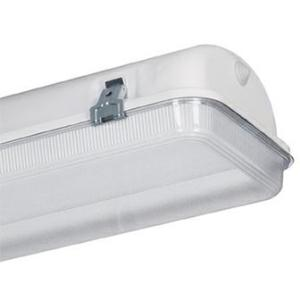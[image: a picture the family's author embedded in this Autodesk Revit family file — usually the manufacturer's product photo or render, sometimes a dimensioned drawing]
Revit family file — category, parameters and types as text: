
# Revit family: 3f_filippi_-_beta_i3f_75_pc_ampio_3f_filippi_-_55596_-_i3f_led_752x12w_ampio_l655
name_source: partatom
category: Lighting Fixtures
units: mm (PartAtom-declared; Revit-internal decimal feet)

## family parameters
Cut with Voids When Loaded = No
Host = Face
Light Source = No
Part Type = Normal
Room Calculation Point = No
Round Connector Dimension = Use Diameter
Shared = No

## types (1)
- 3F Filippi - Beta i3F 75 PC Ampio (1 x LED, 3955 lm, 28 W, 4000 K)
    Apparent Load = 28 VA
    Approval mark = ENEC
    CIE Flux Codes = 52 82 96 97 100
    Color Rendering = 80
    Color Temperature = 4000 K
    Control Gear = Electronic ballast
    Default Elevation = 1800 mm
    Description = ILLUMINOTECHNICAL
Luminous efficiency 100% (DLOR 97%, ULOR 3%).
Initial luminous flux of the luminaire 3955 lm.
Wide symmetric distribution.
Installation Interdistance Transv.D = 1.27 x hu - Long.D = 1.26 x hu.
Tabular UGR (CIE 117 - 4H-8H; S=0.25H; 70/50/20): RUG 20.5 - 22.1.
Beam angle: 92° - 100°.
Luminous efficacy 141 lm/W.
Lifetime (L93/B10): 30000 h. (tq+25°C)
Lifetime (L90/B10): 50000 h. (tq+25°C)
Lifetime (L85/B10): 80000 h. (tq+25°C)
Lifetime (L80/B10): 100000 h. (tq+25°C)
Lifetime (L85/B10): 50000 h. (tq+35°C)
Sudden decreased luminous flux after 50000 hours: 0% (C0).
Photobiological safety in compliance with IEC/TR 62778: RG0 risk exempt, (IEC 62471).
In compliance with IEC/EN 62722-2-1 - IEC/EN 62717 standards.

SOURCE
2 linear LED modules 12W/840.
Energy efficiency class (UE 2019/2020 - UE 2019/2015): D.
CIE 13.3 Colour rendering index: CRI >80 (R9 <50%).
IES TM-30 Fidelity Index: Rf = 84 Rg = 95.
CCT nominal colour temperature 4000 K.
Colour initial tolerance (MacAdam): SDCM 3.

MECHANICAL
Single-piece housing in pressed steel, powder-coated in white epoxy-polyester.
Diffuser in self-extinguishing V2 polycarbonate, photo-engraved interior, UV stabilised, injection moulded, with smooth outer surface, sealing gasket, hinged opening by means of galvanised steel clips.
Wide flow recuperator, oversized, in specular aluminium with superficial titanium-magnesium treatment, non-iridescent.
Gear-tray unit in hot-galvanised steel, painted in white polyester, fixed to the housing by means of "Ribloc" rapid devices in galvanised steel, hinged opening.
Luminaire with limited surface temperature. - D - (EN 60598-2-24)
Dimensions: 655x235 mm, height 140 mm. Weight 3.08 kg.
IP65 protection degree.
Mechanical strength to impacts IK10 (20 joule).
Glow-wire test resistance 850°C.

ELECTRICAL
Halogen Free electronic wiring 230V-50/60Hz, power factor 0.90, THD <25%, constant output current, SELV, class I, 1 driver.
Power of the luminaire 28 W.
CE - IEC 60598-1 - EN 60598-1.
SAFE FLICKER: PstLM=<1 and SVM=<0.4 (IEC TR 61547-1 and IEC TR 63158), to ensure a more comfortable and safe light.
Luminaire compliant with EN 60598-2-22 for power supply from a centralised emergency system CPSS (Central Power Supply System), not incorporated in the luminaire - high risk areas excluded. The default power and flux are 100% in AC and 100% in DC.
Ambient temperature from -20°C to +35°C.
Temperature class T6 max 85°C.
Relative humidity UR: <85%.

INSTALLATION
Ceiling / Suspended / Wall.
All accessories dedicated to this product are available on the Catalog and on our website www.3F-Filippi.com.

APPLICATIONS
Suitable product for food production plants (HACCP), IFS (Food Version 6), BRC (GSFS Food Version 7).
In industrial environments, stores and dry, dusty indoor environments, subject to occasional water splashes.

WARNING
Fixture not suitable for cold stores with an ambient temperature <0°C and/or relative humidity >85%.
Luminaire designed for disposal/recycling at end-of-life.
Replaceable (LED only) light source by a professional. Replaceable control gear by a professional.
    Height = 140 mm  [stored 0.459318 ft]
    Lamp = 1 x LED
    Lamp Light Flux = 3955 lm
    Lamp Power = 28 W
    Lamp count = 1
    Length = 655 mm
    Lifetime = 50000 h
    Luminous efficacy = 141 lm/W
    Manufacturer = 3F Filippi
    ModVariant = No
    Model = 3F Filippi - 55596 - i3F LED 752x12W AMPIO L655
    Mounting Place = Ceiling
    Mounting Type = Pendant
    Number of Poles = 1
    OnlyDefault = Yes
    Power Factor = 1
    Product Name = 3F Filippi - Beta i3F 75 PC Ampio
    Product group = pendant luminaire
    ProductGroupID = 9
    Protection Class = Protection class I
    Protection Degree = IP 65
    RLX_Detail_Level = 1
    RLX_Emergency_Light_Flux = 0 lm
    RLX_Emergency_Type = 0
    RLX_Emergency_Type_DB = No
    RlxData = <blob elided: 65613 chars, md5=47a6b991>
    Socket = socket
    Standby Power = 0 W
    System Light Flux = 3955 lm
    System Power = 28 W
    Type Comments = Product without accessories
    Type Image = 3ffilippi_55596.jpg
    URL = http://relux.com
    VarID = ---
    Voltage = 0 V
    Weight = 0.00 kg
    Width = 235 mm

note: [stored X ft] marks values corroborated as IEEE doubles in the binary element streams (Revit-internal decimal feet)

## geometry (parser evidence)
native form markers: Blend x4, Sweep x10
no freeform markers — native parametric forms only
